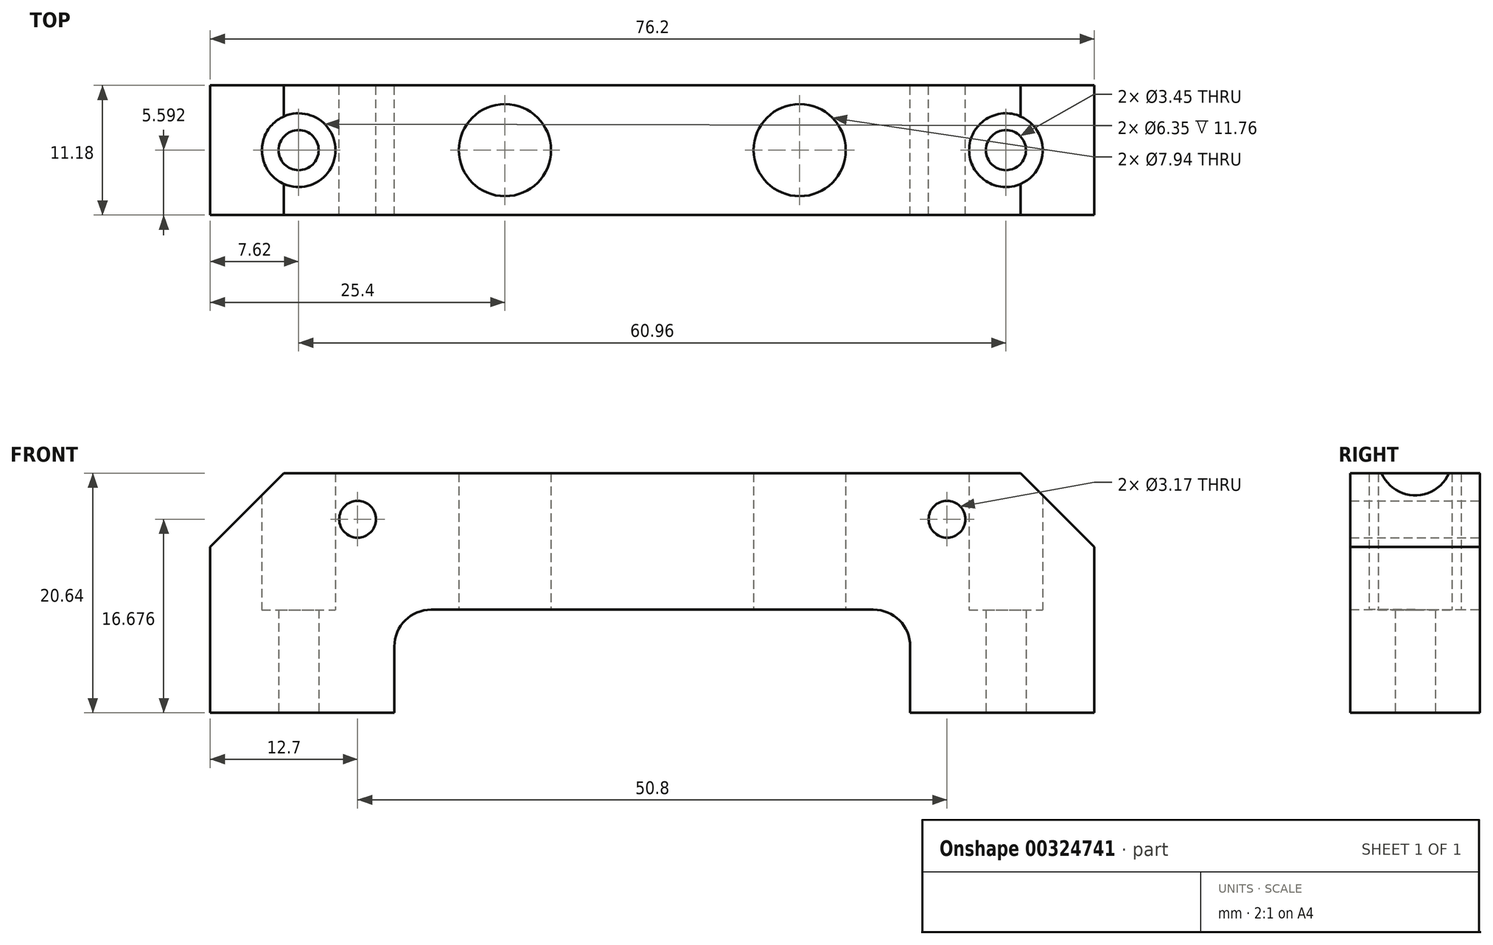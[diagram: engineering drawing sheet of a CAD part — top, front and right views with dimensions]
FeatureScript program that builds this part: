
annotation { "Feature Type Name" : "Feature", "Feature Type Description" : "" }
export const myFeature = defineFeature(function(context is Context, id is Id, definition is map)
    precondition{}
    {
        {
            var Q0;
            Q0=qCreatedBy(makeId("Front.planeOp"),FACE);
            var sketch = newSketch(context, id + "F0", { "sketchPlane" : qUnion([Q0])});
            skLineSegment(sketch, "E0.bottom", {"start": v(-38.1, 10.32) * mm, "end": v(38.1, 10.32) * mm});
            skLineSegment(sketch, "E0.top", {"start": v(-38.1, -10.32) * mm, "end": v(-22.23, -10.32) * mm});
            skLineSegment(sketch, "E0.left", {"start": v(-38.1, 10.32) * mm, "end": v(-38.1, -10.32) * mm});
            skLineSegment(sketch, "E0.right", {"start": v(38.1, 10.32) * mm, "end": v(38.1, -10.32) * mm});
            skPoint(sketch, "E0.middle", {"position": v(0, 0) * mm});
            skLineSegment(sketch, "E1.top", {"start": v(-22.23, -1.43) * mm, "end": v(22.23, -1.43) * mm});
            skLineSegment(sketch, "E1.left", {"start": v(-22.23, -10.32) * mm, "end": v(-22.23, -1.43) * mm});
            skLineSegment(sketch, "E1.right", {"start": v(22.23, -10.32) * mm, "end": v(22.23, -1.43) * mm});
            skLineSegment(sketch, "E2.trimOffspring", {"start": v(22.23, -10.32) * mm, "end": v(38.1, -10.32) * mm});
            skSolve(sketch);
        }
        {
            var Q0;
            Q0=makeQuery(id+"F0.imprint","IMPRINT",FACE,{"disambiguationData":[TD([[makeQuery(id+"F0.imprint","IMPRINT",EDGE,{"derivedFrom":sQuery(id+"F0.wireOp",EDGE,"E0.bottom")}),-1.0]])]});
            extrude(context, id + "F1", {"entities" : qUnion([Q0]), "depth" : 11.18 * mm, "offsetDistance" : 25.4 * mm});
        }
        {
            var Q0;
            Q0=makeQuery(id+"F1.opExtrude","SWEPT_EDGE",EDGE,{"disambiguationData":[OSD([sQuery(id+"F0.wireOp",EDGE,"E1.top"),sQuery(id+"F0.wireOp",EDGE,"E1.left")])]});
            var Q1;
            Q1=makeQuery(id+"F1.opExtrude","SWEPT_EDGE",EDGE,{"disambiguationData":[OSD([sQuery(id+"F0.wireOp",EDGE,"E1.top"),sQuery(id+"F0.wireOp",EDGE,"E1.right")])]});
            fillet(context, id + "F2", {"entities" : qUnion([Q0, Q1]), "radius" : 3.17 * mm, "tangentPropagation" : true, "allowEdgeOverflow" : false});
        }
        {
            var Q0;
            Q0=qCreatedBy(makeId("Top.planeOp"),FACE);
            cPlane(context, id + "F3", {"entities" : qUnion([Q0]), "cplaneType" : CPlaneType.OFFSET, "offset" : 20.65 * mm, "width" : 152.4 * mm, "height" : 152.4 * mm});
        }
        {
            var Q0;
            Q0=qCreatedBy(id+"F3.planeOp",FACE);
            var sketch = newSketch(context, id + "F4", { "sketchPlane" : qUnion([Q0])});
            skPoint(sketch, "E3", {"position": v(-30.48, -5.59) * mm});
            skPoint(sketch, "E4", {"position": v(30.48, -5.59) * mm});
            skSolve(sketch);
        }
        {
            var Q0;
            Q0=sQuery(id+"F4.wireOp",VERTEX,"E3");
            var Q1;
            Q1=sQuery(id+"F4.wireOp",VERTEX,"E4");
            var Q2;
            Q2=makeQuery(id+"F1.opExtrude","SWEPT_BODY",BODY,{"disambiguationData":[OSD([sQuery(id+"F0.wireOp",EDGE,"E0.bottom"),sQuery(id+"F0.wireOp",EDGE,"E0.top"),sQuery(id+"F0.wireOp",EDGE,"E0.left"),sQuery(id+"F0.wireOp",EDGE,"E0.right"),sQuery(id+"F0.wireOp",EDGE,"E1.top"),sQuery(id+"F0.wireOp",EDGE,"E1.left"),sQuery(id+"F0.wireOp",EDGE,"E1.right"),sQuery(id+"F0.wireOp",EDGE,"E2.trimOffspring")])]});
            hole(context, id + "F5", {"style" : HoleStyle.C_BORE, "endStyle" : HoleEndStyle.THROUGH, "holeDiameter" : 3.45 * mm, "cBoreDiameter" : 6.35 * mm, "cBoreDepth" : 11.76 * mm, "majorDiameter" : 6.35 * mm, "isTappedThrough" : true, "tappedDepth" : 12.7 * mm, "tapClearance" : 3, "locations" : qUnion([Q0, Q1]), "scope" : qUnion([Q2])});
        }
        {
            var Q0;
            Q0=makeQuery(id+"F1.opExtrude","SWEPT_EDGE",EDGE,{"disambiguationData":[OSD([sQuery(id+"F0.wireOp",EDGE,"E0.bottom"),sQuery(id+"F0.wireOp",EDGE,"E0.left")])]});
            var Q1;
            Q1=makeQuery(id+"F1.opExtrude","SWEPT_EDGE",EDGE,{"disambiguationData":[OSD([sQuery(id+"F0.wireOp",EDGE,"E0.bottom"),sQuery(id+"F0.wireOp",EDGE,"E0.right")])]});
            chamfer(context, id + "F6", {"entities" : qUnion([Q0, Q1]), "width" : 6.35 * mm, "tangentPropagation" : true});
        }
        {
            var Q0;
            Q0=qCreatedBy(id+"F3.planeOp",FACE);
            var sketch = newSketch(context, id + "F7", { "sketchPlane" : qUnion([Q0])});
            skPoint(sketch, "E5", {"position": v(-12.7, -5.59) * mm});
            skPoint(sketch, "E6", {"position": v(12.7, -5.59) * mm});
            skSolve(sketch);
        }
        {
            var Q0;
            Q0=sQuery(id+"F7.wireOp",VERTEX,"E5");
            var Q1;
            Q1=sQuery(id+"F7.wireOp",VERTEX,"E6");
            var Q2;
            Q2=makeQuery(id+"F1.opExtrude","SWEPT_BODY",BODY,{"disambiguationData":[OSD([sQuery(id+"F0.wireOp",EDGE,"E0.bottom"),sQuery(id+"F0.wireOp",EDGE,"E0.top"),sQuery(id+"F0.wireOp",EDGE,"E0.left"),sQuery(id+"F0.wireOp",EDGE,"E0.right"),sQuery(id+"F0.wireOp",EDGE,"E1.top"),sQuery(id+"F0.wireOp",EDGE,"E1.left"),sQuery(id+"F0.wireOp",EDGE,"E1.right"),sQuery(id+"F0.wireOp",EDGE,"E2.trimOffspring")])]});
            hole(context, id + "F8", {"style" : HoleStyle.SIMPLE, "endStyle" : HoleEndStyle.THROUGH, "holeDiameter" : 7.94 * mm, "majorDiameter" : 6.35 * mm, "isTappedThrough" : true, "tappedDepth" : 12.7 * mm, "tapClearance" : 3, "locations" : qUnion([Q0, Q1]), "scope" : qUnion([Q2])});
        }
        {
            var Q0;
            Q0=makeQuery(id+"F1.opExtrude","CAP_FACE",FACE,{"disambiguationData":[OSD([sQuery(id+"F0.wireOp",EDGE,"E0.bottom"),sQuery(id+"F0.wireOp",EDGE,"E0.top"),sQuery(id+"F0.wireOp",EDGE,"E0.left"),sQuery(id+"F0.wireOp",EDGE,"E0.right"),sQuery(id+"F0.wireOp",EDGE,"E1.top"),sQuery(id+"F0.wireOp",EDGE,"E1.left"),sQuery(id+"F0.wireOp",EDGE,"E1.right"),sQuery(id+"F0.wireOp",EDGE,"E2.trimOffspring")])],"isStart":false});
            var sketch = newSketch(context, id + "F9", { "sketchPlane" : qUnion([Q0])});
            skLineSegment(sketch, "E7", {"start": v(-71.59, 6.36) * mm, "end": v(71.68, 6.36) * mm});
            skPoint(sketch, "E8", {"position": v(-25.4, 6.36) * mm});
            skPoint(sketch, "E9", {"position": v(25.4, 6.36) * mm});
            skSolve(sketch);
        }
        {
            var Q0;
            Q0=sQuery(id+"F9.wireOp",VERTEX,"E8");
            var Q1;
            Q1=sQuery(id+"F9.wireOp",VERTEX,"E9");
            var Q2;
            Q2=makeQuery(id+"F1.opExtrude","SWEPT_BODY",BODY,{"disambiguationData":[OSD([sQuery(id+"F0.wireOp",EDGE,"E0.bottom"),sQuery(id+"F0.wireOp",EDGE,"E0.top"),sQuery(id+"F0.wireOp",EDGE,"E0.left"),sQuery(id+"F0.wireOp",EDGE,"E0.right"),sQuery(id+"F0.wireOp",EDGE,"E1.top"),sQuery(id+"F0.wireOp",EDGE,"E1.left"),sQuery(id+"F0.wireOp",EDGE,"E1.right"),sQuery(id+"F0.wireOp",EDGE,"E2.trimOffspring")])]});
            hole(context, id + "F10", {"style" : HoleStyle.SIMPLE, "endStyle" : HoleEndStyle.THROUGH, "holeDiameter" : 3.17 * mm, "majorDiameter" : 6.35 * mm, "isTappedThrough" : true, "tappedDepth" : 12.7 * mm, "tapClearance" : 3, "locations" : qUnion([Q0, Q1]), "scope" : qUnion([Q2])});
        }
    });
